# Revit family: RN 80026 Optipress-Aquaplus-Verschlusskappe
name_source: partatom
category: Rohrformteile
units: mm (PartAtom-declared; Revit-internal decimal feet)

## family parameters
Arbeitsebenenbasiert = Nein
Beim Laden mit Abzugskörper schneiden = Nein
Bemaßung runder Anschluss = Durchmesser verwenden
Gemeinsam genutzt = Nein
Immer vertikal = Ja
Teiletyp = Nicht definiert

## types (7) — shared parameters
1.010.00.2 Blattnummer der Richtlinie = 29
1.010.00.3 Ausgabedatum (Monat) der Richtlinie = 201308
1.010.00.4 Herstellername = R. Nussbaum AG
1.010.00.5 Revisionsdatum der Datei = 20190521
1.010.00.6 Webadresse des Herstellers = http://www.nussbaum.ch
1.100.00.4 Produktbezeichnung = Versorgung
1.110.00.2 Index = 4
1.110.00.4 Produktbezeichnung = Optipress
1.960/3L.00.8 Link (URL) = https://www.nussbaum.ch
29.700.00.4 Produktname = Optipress-Aquaplus-Verschlusskappe, mit Innengewinde exzentrisch
29.700.00.5 Produktkennung = 2
29.700.00.6 Querschnittsform = 1
29.700.00.7 Nennweitensystem = DN
29.700.00.8 Nenndrucksystem = PN
29.710.02.4 Nenndruck = 16
29.710.02.5 max. zul. Überdruck [hPa] = 1600
29.710.02.7 max. zul. Dauer-Betriebsdruck [hPa] = 1600
29.710.02.9 max. zul. Dauer-Betriebstemperatur [°C] = 95
Connector Visibility = Nein
EnclosingSpace Visibility = Nein

## per-type parameters (varying)
| type | 1.800.00.3 TGA-Nummer | 1.810.00.3 Hersteller-Bestellnummer | 1.810.00.4 DATANORM-Nummer | 1.810.00.5 StLB-Nummer | 1.810.00.6 GTIN-Nummer | 29.710.02.10 Formstück-Gewicht [kg] | 29.710.02.3 Benennung | CONNECTOR0_DIAMETER_dX_0r | CONNECTOR0_dX_01 | CONNECTOR0_ref_dX | CONNECTOR1_DIAMETER_dX_0r | CONNECTOR1_dX_00 | CONNECTOR1_dX_01 | CONNECTOR1_ref_dX | CONNECTOR1_ref_dZ | R. Nussbaum AG 80026.26 de Visibility | R. Nussbaum AG 80026.27 de Visibility | R. Nussbaum AG 80026.28 de Visibility | R. Nussbaum AG 80026.70 de Visibility | R. Nussbaum AG 80026.71 de Visibility | R. Nussbaum AG 80026.72 de Visibility | R. Nussbaum AG 80026.73 de Visibility |
| 80026.26, Optipress-Aquaplus-Verschlusskappe, mit Innengewinde exzentrisch, DN=32, L=50, Rp=½ | 01900400000000000000000000000000000000000000000019000000000000000002 | 80026.26 | 80026.26 |  | 7612945689924 | 0.095 | Optipress-Aquaplus-Verschlusskappe, mit Innengewinde exzentrisch, DN=32, L=50, Rp=½ | 32 mm | 26 mm | 26 mm | 15 mm  [stored 0.0492126 ft] | 40 mm | 50 mm | 40 mm | 2 mm  [stored 0.00656168 ft] | Ja | Nein | Nein | Nein | Nein | Nein | Nein |
| 80026.27, Optipress-Aquaplus-Verschlusskappe, mit Innengewinde exzentrisch, DN=40, L=62, Rp=½ | 01900400000000000000000000000000000000000000000019000000000000000003 | 80026.27 | 80026.27 |  | 7612945689931 | 0.142 | Optipress-Aquaplus-Verschlusskappe, mit Innengewinde exzentrisch, DN=40, L=62, Rp=½ | 40 mm | 36 mm | 36 mm | 15 mm  [stored 0.0492126 ft] | 52 mm | 62 mm | 52 mm | 5 mm  [stored 0.0164042 ft] | Nein | Ja | Nein | Nein | Nein | Nein | Nein |
| 80026.28, Optipress-Aquaplus-Verschlusskappe, mit Innengewinde exzentrisch, DN=50, L=67, Rp=½ | 01900400000000000000000000000000000000000000000019000000000000000004 | 80026.28 | 80026.28 |  | 7612945689948 | 0.201 | Optipress-Aquaplus-Verschlusskappe, mit Innengewinde exzentrisch, DN=50, L=67, Rp=½ | 50 mm | 40 mm | 40 mm | 15 mm  [stored 0.0492126 ft] | 57 mm | 67 mm | 57 mm | 11 mm | Nein | Nein | Ja | Nein | Nein | Nein | Nein |
| 80026.71, Optipress-Aquaplus-Verschlusskappe, mit Innengewinde exzentrisch, DN=65, L=105, Rp=¾ | 01900400000000000000000000000000000000000000000019000000000000000005 | 80026.71 | 80026.71 | 265.521 | 7612945655486 | 0.469 | Optipress-Aquaplus-Verschlusskappe, mit Innengewinde exzentrisch, DN=65, L=105, Rp=¾ | 65 mm | 50 mm | 50 mm | 20 mm | 95 mm | 105 mm | 95 mm | 14 mm  [stored 0.0459318 ft] | Nein | Nein | Nein | Nein | Ja | Nein | Nein |
| 80026.72, Optipress-Aquaplus-Verschlusskappe, mit Innengewinde exzentrisch, DN=80, L=105, Rp=¾ | 01900400000000000000000000000000000000000000000019000000000000000006 | 80026.72 | 80026.72 | 265.522 | 7612945655493 | 0.546 | Optipress-Aquaplus-Verschlusskappe, mit Innengewinde exzentrisch, DN=80, L=105, Rp=¾ | 80 mm | 50 mm | 50 mm | 20 mm | 95 mm | 105 mm | 95 mm | 20 mm | Nein | Nein | Nein | Nein | Nein | Ja | Nein |
| 80026.73, Optipress-Aquaplus-Verschlusskappe, mit Innengewinde exzentrisch, DN=100, L=115, Rp=¾ | 01900400000000000000000000000000000000000000000019000000000000000007 | 80026.73 | 80026.73 | 265.523 | 7612945655509 | 0.746 | Optipress-Aquaplus-Verschlusskappe, mit Innengewinde exzentrisch, DN=100, L=115, Rp=¾ | 100 mm  [stored 0.328084 ft] | 60 mm | 60 mm | 20 mm | 105 mm | 115 mm | 105 mm | 29 mm | Nein | Nein | Nein | Nein | Nein | Nein | Ja |
| 80026.70, Optipress-Aquaplus-Verschlusskappe, mit Innengewinde exzentrisch, DN=60, L=99, Rp=¾ | 01900400000000000000000000000000000000000000000019000000000000000008 | 80026.70 | 80026.70 | 265.524 | 7612945667137 | 0.359 | Optipress-Aquaplus-Verschlusskappe, mit Innengewinde exzentrisch, DN=60, L=99, Rp=¾ | 60 mm | 43 mm  [stored 0.141076 ft] | 43 mm  [stored 0.141076 ft] | 20 mm | 89 mm | 99 mm | 89 mm | 8 mm  [stored 0.0262467 ft] | Nein | Nein | Nein | Ja | Nein | Nein | Nein |

note: column(s) folded — value = type name in every type: 1.800.00.4 Kommentarfeld

note: [stored X ft] marks values corroborated as IEEE doubles in the binary element streams (Revit-internal decimal feet)

## geometry (parser evidence)
native form markers: Sweep x2
no freeform markers — native parametric forms only
